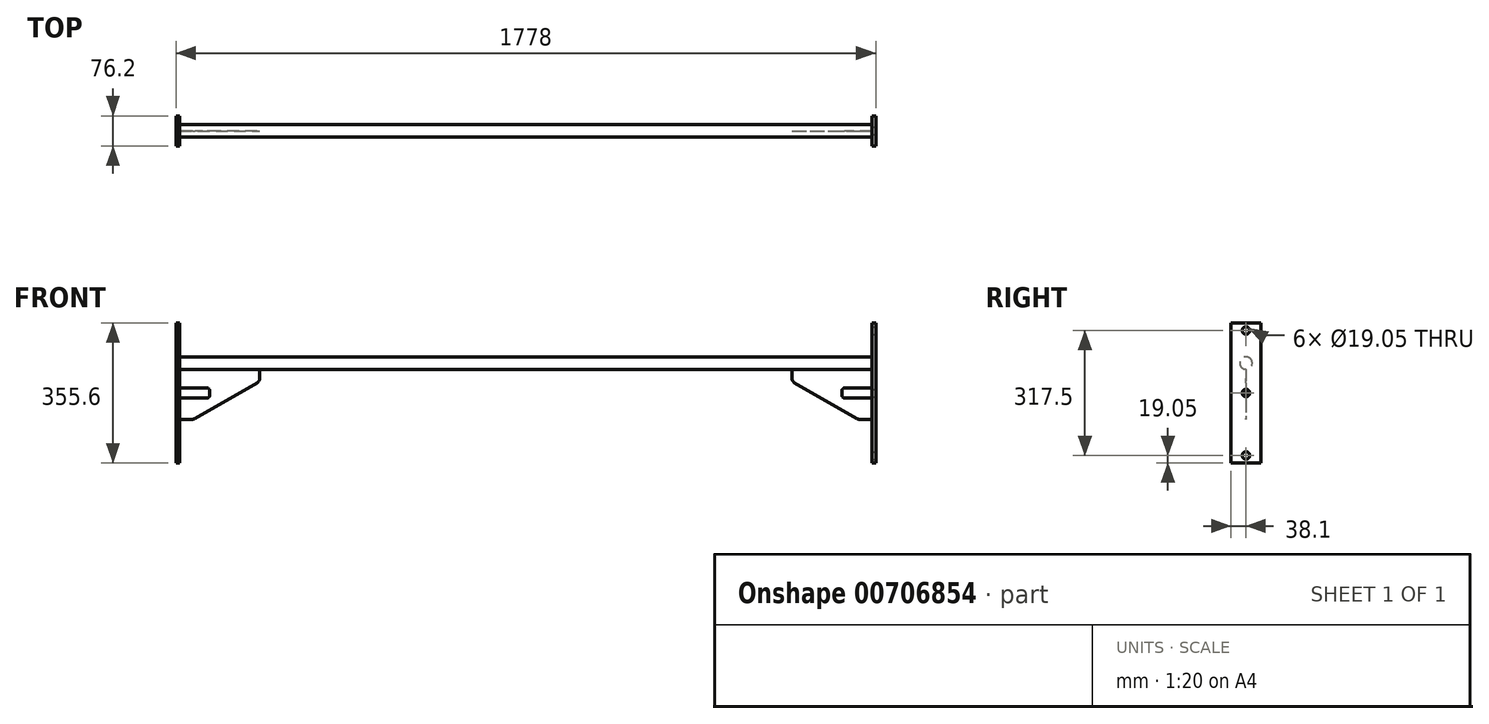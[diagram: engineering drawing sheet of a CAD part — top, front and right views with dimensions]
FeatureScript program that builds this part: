
annotation { "Feature Type Name" : "Feature", "Feature Type Description" : "" }
export const myFeature = defineFeature(function(context is Context, id is Id, definition is map)
    precondition{}
    {
        {
            var Q0;
            Q0=qCreatedBy(makeId("Front.planeOp"),FACE);
            var sketch = newSketch(context, id + "F0", { "sketchPlane" : qUnion([Q0])});
            skLineSegment(sketch, "E0.bottom", {"start": v(-889, 177.8) * mm, "end": v(-879.48, 177.8) * mm});
            skLineSegment(sketch, "E0.top", {"start": v(-889, -177.8) * mm, "end": v(-879.48, -177.8) * mm});
            skLineSegment(sketch, "E0.left", {"start": v(-889, 177.8) * mm, "end": v(-889, -177.8) * mm});
            skLineSegment(sketch, "E0.right", {"start": v(-879.48, 177.8) * mm, "end": v(-879.48, -177.8) * mm});
            skLineSegment(sketch, "E1.MirrorCS", {"start": v(879.48, 177.8) * mm, "end": v(879.48, -177.8) * mm});
            skLineSegment(sketch, "E2.MirrorCS", {"start": v(889, 177.8) * mm, "end": v(889, -177.8) * mm});
            skLineSegment(sketch, "E3.MirrorCS", {"start": v(889, 177.8) * mm, "end": v(879.48, 177.8) * mm});
            skLineSegment(sketch, "E4.MirrorCS", {"start": v(889, -177.8) * mm, "end": v(879.48, -177.8) * mm});
            skSolve(sketch);
        }
        {
            var Q0;
            Q0 = qSketchRegion(id + "F0", true);
            extrude(context, id + "F1", {"entities" : qUnion([Q0]), "depth" : 38.1 * mm, "offsetDistance" : 25 * mm, "hasSecondDirection" : true, "secondDirectionOppositeDirection" : true, "secondDirectionDepth" : 38.1 * mm});
        }
        {
            var Q0;
            Q0=qCreatedBy(makeId("Right.planeOp"),FACE);
            var sketch = newSketch(context, id + "F2", { "sketchPlane" : qUnion([Q0])});
            skCircle(sketch, "E5", {"center": v(0, 76.2) * mm, "radius": 15.88 * mm});
            skSolve(sketch);
        }
        {
            var Q0;
            Q0 = qSketchRegion(id + "F2", true);
            extrude(context, id + "F3", {"entities" : qUnion([Q0]), "endBound" : BoundingType.UP_TO_NEXT, "depth" : 25.4 * mm, "offsetDistance" : 25.4 * mm, "hasSecondDirection" : true, "secondDirectionBound" : SecondDirectionBoundingType.UP_TO_NEXT, "secondDirectionOppositeDirection" : true, "secondDirectionDepth" : 25.4 * mm});
        }
        {
            var Q0;
            Q0=makeQuery(id+"F1.opExtrude","SWEPT_FACE",FACE,{"disambiguationData":[OSD([sQuery(id+"F0.wireOp",EDGE,"E2.MirrorCS")])]});
            var sketch = newSketch(context, id + "F4", { "sketchPlane" : qUnion([Q0])});
            skCircle(sketch, "E6", {"center": v(0, -158.75) * mm, "radius": 9.52 * mm});
            skCircle(sketch, "E7", {"center": v(0, 0) * mm, "radius": 9.52 * mm});
            skCircle(sketch, "E8", {"center": v(0, 158.75) * mm, "radius": 9.52 * mm});
            skSolve(sketch);
        }
        {
            var Q0;
            Q0 = qSketchRegion(id + "F4", true);
            extrude(context, id + "F5", {"entities" : qUnion([Q0]), "operationType" : NewBodyOperationType.REMOVE, "endBound" : BoundingType.THROUGH_ALL, "oppositeDirection" : true, "depth" : 25.4 * mm, "offsetDistance" : 25.4 * mm});
        }
        {
            var Q0;
            Q0=qCreatedBy(makeId("Front.planeOp"),FACE);
            var sketch = newSketch(context, id + "F6", { "sketchPlane" : qUnion([Q0])});
            skLineSegment(sketch, "E9", {"start": v(879.48, 60.33) * mm, "end": v(-879.47, 60.33) * mm, "construction": true});
            skLineSegment(sketch, "E10.0", {"start": v(879.48, 177.8) * mm, "end": v(879.48, -177.8) * mm});
            skLineSegment(sketch, "E11", {"start": v(889, -9.53) * mm, "end": v(879.47, -9.52) * mm});
            skLineSegment(sketch, "E12", {"start": v(879.47, 9.52) * mm, "end": v(889, 9.52) * mm});
            skLineSegment(sketch, "E13.0", {"start": v(879.47, 9.52) * mm, "end": v(879.47, -9.52) * mm, "construction": true});
            skLineSegment(sketch, "E14", {"start": v(676.27, 60.33) * mm, "end": v(676.27, 37) * mm});
            skLineSegment(sketch, "E15", {"start": v(682.62, 26) * mm, "end": v(840.2, -64.97) * mm});
            skLineSegment(sketch, "E16", {"start": v(846.55, -66.67) * mm, "end": v(879.48, -66.67) * mm});
            skLineSegment(sketch, "E17.bottom", {"start": v(879.48, 12.7) * mm, "end": v(809.62, 12.7) * mm});
            skLineSegment(sketch, "E17.top", {"start": v(879.48, -12.7) * mm, "end": v(809.62, -12.7) * mm});
            skLineSegment(sketch, "E17.left", {"start": v(879.48, 12.7) * mm, "end": v(879.48, -12.7) * mm});
            skLineSegment(sketch, "E17.right", {"start": v(803.27, 6.35) * mm, "end": v(803.27, -6.35) * mm});
            skPoint(sketch, "E18.0", {"position": v(889, 0) * mm});
            skLineSegment(sketch, "E19", {"start": v(1096.63, 0) * mm, "end": v(577.07, 0) * mm, "construction": true});
            skPoint(sketch, "E20.visualSharp", {"position": v(803.27, -12.7) * mm});
            skArc(sketch, "E20.filletArc", {"start": v(803.27, -6.35) * mm, "mid": v(805.13, -10.84) * mm, "end": v(809.62, -12.7) * mm});
            skPoint(sketch, "E21.visualSharp", {"position": v(803.27, 12.7) * mm});
            skArc(sketch, "E21.filletArc", {"start": v(809.62, 12.7) * mm, "mid": v(805.13, 10.84) * mm, "end": v(803.28, 6.35) * mm});
            skLineSegment(sketch, "E22", {"start": v(879.48, -66.67) * mm, "end": v(879.48, 60.33) * mm});
            skLineSegment(sketch, "E23", {"start": v(676.27, 60.33) * mm, "end": v(879.48, 60.33) * mm});
            skPoint(sketch, "E24.visualSharp", {"position": v(676.27, 29.67) * mm});
            skArc(sketch, "E24.filletArc", {"start": v(676.27, 37) * mm, "mid": v(677.98, 30.65) * mm, "end": v(682.62, 26) * mm});
            skPoint(sketch, "E25.visualSharp", {"position": v(843.15, -66.67) * mm});
            skArc(sketch, "E25.filletArc", {"start": v(840.2, -64.97) * mm, "mid": v(843.27, -66.24) * mm, "end": v(846.55, -66.67) * mm});
            skLineSegment(sketch, "E26.MirrorCS", {"start": v(-676.27, 60.33) * mm, "end": v(-676.27, 37) * mm});
            skLineSegment(sketch, "E27.MirrorCS", {"start": v(-682.62, 26) * mm, "end": v(-840.2, -64.97) * mm});
            skArc(sketch, "E28.MirrorCS", {"start": v(-676.27, 37) * mm, "mid": v(-677.98, 30.65) * mm, "end": v(-682.62, 26) * mm});
            skArc(sketch, "E29.MirrorCS", {"start": v(-840.2, -64.97) * mm, "mid": v(-843.27, -66.24) * mm, "end": v(-846.55, -66.67) * mm});
            skLineSegment(sketch, "E30.MirrorCS", {"start": v(-846.55, -66.67) * mm, "end": v(-879.48, -66.67) * mm});
            skLineSegment(sketch, "E31.MirrorCS", {"start": v(-879.48, -12.7) * mm, "end": v(-809.62, -12.7) * mm});
            skArc(sketch, "E32.MirrorCS", {"start": v(-803.27, -6.35) * mm, "mid": v(-805.13, -10.84) * mm, "end": v(-809.62, -12.7) * mm});
            skLineSegment(sketch, "E33.MirrorCS", {"start": v(-803.27, 6.35) * mm, "end": v(-803.27, -6.35) * mm});
            skArc(sketch, "E34.MirrorCS", {"start": v(-809.62, 12.7) * mm, "mid": v(-805.13, 10.84) * mm, "end": v(-803.28, 6.35) * mm});
            skLineSegment(sketch, "E35.MirrorCS", {"start": v(-879.48, 12.7) * mm, "end": v(-809.62, 12.7) * mm});
            skLineSegment(sketch, "E36.MirrorCS", {"start": v(-879.48, 177.8) * mm, "end": v(-879.48, -177.8) * mm});
            skLineSegment(sketch, "E37.MirrorCS", {"start": v(-879.48, 60.33) * mm, "end": v(879.47, 60.33) * mm, "construction": true});
            skLineSegment(sketch, "E38", {"start": v(-879.47, 60.33) * mm, "end": v(-676.27, 60.33) * mm});
            skSolve(sketch);
        }
        {
            var Q0;
            Q0=makeQuery(id+"F6.imprint","IMPRINT",FACE,{"disambiguationData":[TD([[makeQuery(id+"F6.imprint","IMPRINT",EDGE,{"derivedFrom":sQuery(id+"F6.wireOp",EDGE,"E14")}),1.0]])]});
            var Q1;
            Q1=makeQuery(id+"F6.imprint","IMPRINT",FACE,{"disambiguationData":[TD([[makeQuery(id+"F6.imprint","IMPRINT",EDGE,{"derivedFrom":sQuery(id+"F6.wireOp",EDGE,"E26.MirrorCS")}),-1.0]])]});
            extrude(context, id + "F7", {"entities" : qUnion([Q0, Q1]), "depth" : 1.5 / 203.2 * mm, "offsetDistance" : 25.4 * mm, "hasSecondDirection" : true, "secondDirectionOppositeDirection" : true, "secondDirectionDepth" : 1.5 / 203.2 * mm});
        }
    });
